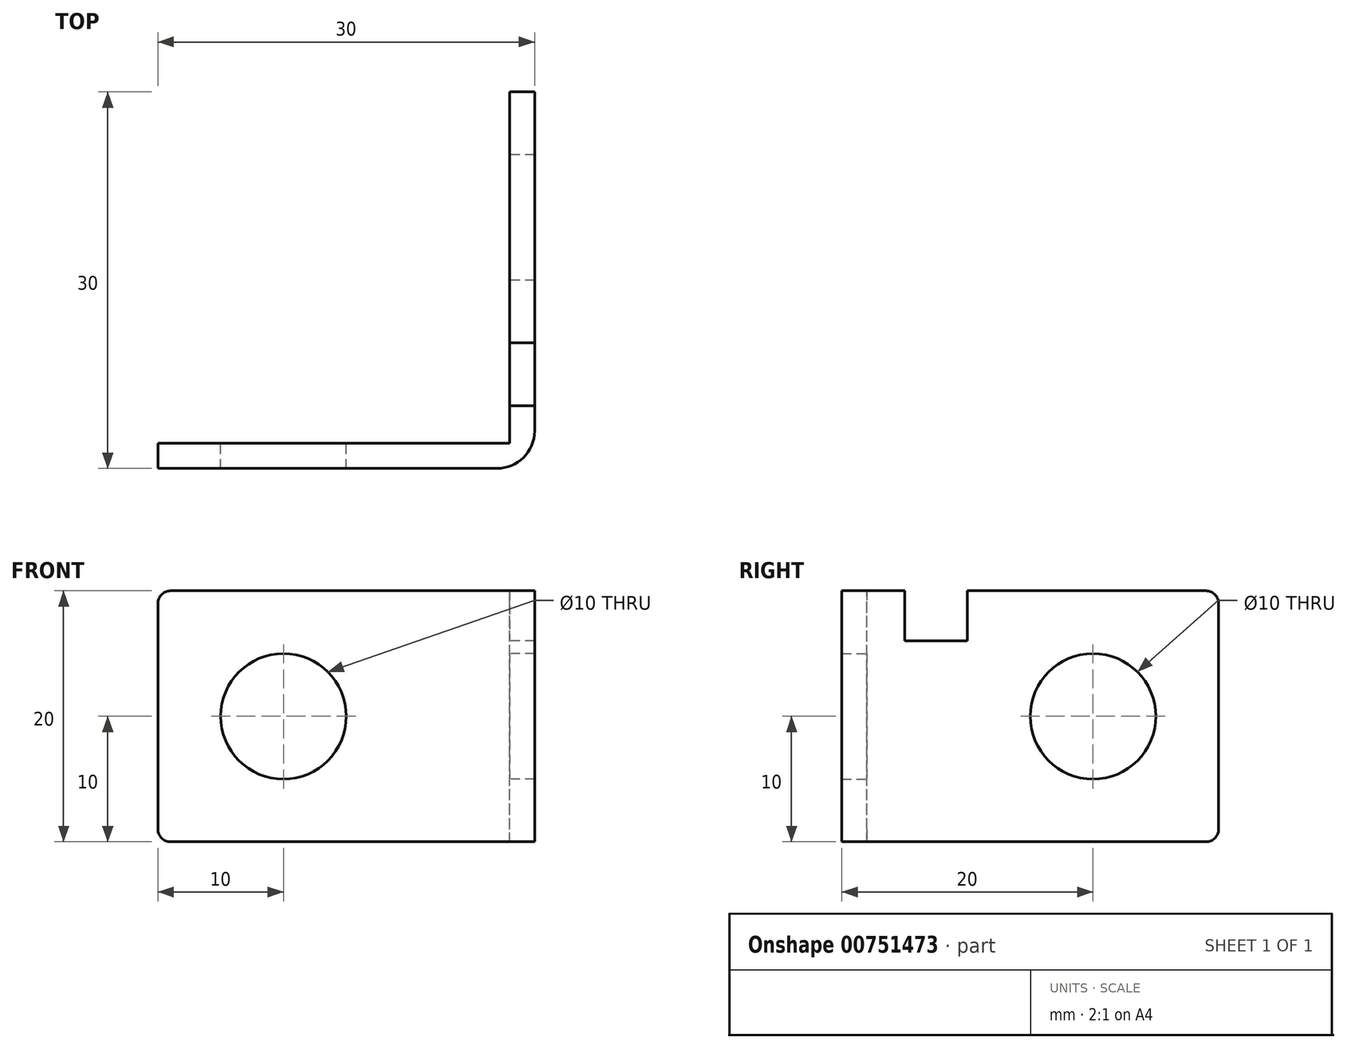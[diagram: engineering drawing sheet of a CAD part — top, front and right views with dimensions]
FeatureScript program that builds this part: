
annotation { "Feature Type Name" : "Feature", "Feature Type Description" : "" }
export const myFeature = defineFeature(function(context is Context, id is Id, definition is map)
    precondition{}
    {
        {
            var Q0;
            Q0=qCreatedBy(makeId("Front.planeOp"),FACE);
            var sketch = newSketch(context, id + "F0", { "sketchPlane" : qUnion([Q0])});
            skLineSegment(sketch, "E0.bottom", {"start": v(0, 0) * mm, "end": v(30, 0) * mm});
            skLineSegment(sketch, "E0.top", {"start": v(0, 20) * mm, "end": v(30, 20) * mm});
            skLineSegment(sketch, "E0.left", {"start": v(0, 0) * mm, "end": v(0, 20) * mm});
            skLineSegment(sketch, "E0.right", {"start": v(30, 0) * mm, "end": v(30, 20) * mm});
            skSolve(sketch);
        }
        {
            var Q0;
            Q0=makeQuery(id+"F0.imprint","IMPRINT",FACE,{"disambiguationData":[TD([[makeQuery(id+"F0.imprint","IMPRINT",EDGE,{"derivedFrom":sQuery(id+"F0.wireOp",EDGE,"E0.bottom")}),1.0]])]});
            extrude(context, id + "F1", {"entities" : qUnion([Q0]), "oppositeDirection" : true, "depth" : 2 * mm, "offsetDistance" : 25 * mm});
        }
        {
            var Q0;
            Q0=makeQuery(id+"F1.opExtrude","CAP_FACE",FACE,{"disambiguationData":[OSD([sQuery(id+"F0.wireOp",EDGE,"E0.bottom"),sQuery(id+"F0.wireOp",EDGE,"E0.top"),sQuery(id+"F0.wireOp",EDGE,"E0.left"),sQuery(id+"F0.wireOp",EDGE,"E0.right")])],"isStart":false});
            var sketch = newSketch(context, id + "F2", { "sketchPlane" : qUnion([Q0])});
            skLineSegment(sketch, "E1.bottom", {"start": v(-30, 0) * mm, "end": v(-28, 0) * mm});
            skLineSegment(sketch, "E1.top", {"start": v(-30, 20) * mm, "end": v(-28, 20) * mm});
            skLineSegment(sketch, "E1.left", {"start": v(-30, 0) * mm, "end": v(-30, 20) * mm});
            skLineSegment(sketch, "E1.right", {"start": v(-28, 0) * mm, "end": v(-28, 20) * mm});
            skSolve(sketch);
        }
        {
            var Q0;
            Q0 = qSketchRegion(id + "F2", true);
            extrude(context, id + "F3", {"entities" : qUnion([Q0]), "operationType" : NewBodyOperationType.ADD, "depth" : 28 * mm, "offsetDistance" : 25 * mm});
        }
        {
            var Q0;
            Q0=makeQuery(id+"F1.opExtrude","CAP_FACE",FACE,{"disambiguationData":[OSD([sQuery(id+"F0.wireOp",EDGE,"E0.bottom"),sQuery(id+"F0.wireOp",EDGE,"E0.top"),sQuery(id+"F0.wireOp",EDGE,"E0.left"),sQuery(id+"F0.wireOp",EDGE,"E0.right")])],"isStart":false});
            var sketch = newSketch(context, id + "F4", { "sketchPlane" : qUnion([Q0])});
            skCircle(sketch, "E2", {"center": v(-10, 10) * mm, "radius": 5 * mm});
            skSolve(sketch);
        }
        {
            var Q0;
            Q0 = qSketchRegion(id + "F4", true);
            extrude(context, id + "F5", {"entities" : qUnion([Q0]), "operationType" : NewBodyOperationType.REMOVE, "endBound" : BoundingType.UP_TO_NEXT, "oppositeDirection" : true, "depth" : 25 * mm, "offsetDistance" : 25 * mm});
        }
        {
            var Q0;
            Q0=makeQuery(id+"F3.opExtrude","SWEPT_FACE",FACE,{"disambiguationData":[OSD([sQuery(id+"F2.wireOp",EDGE,"E1.right")])]});
            var sketch = newSketch(context, id + "F6", { "sketchPlane" : qUnion([Q0])});
            skCircle(sketch, "E3", {"center": v(-20, 10) * mm, "radius": 5 * mm});
            skSolve(sketch);
        }
        {
            var Q0;
            Q0 = qSketchRegion(id + "F6", true);
            extrude(context, id + "F7", {"entities" : qUnion([Q0]), "operationType" : NewBodyOperationType.REMOVE, "endBound" : BoundingType.UP_TO_NEXT, "oppositeDirection" : true, "depth" : 25 * mm, "offsetDistance" : 25 * mm});
        }
        {
            var Q0;
            Q0=makeQuery(id+"F3.opExtrude","SWEPT_FACE",FACE,{"disambiguationData":[OSD([sQuery(id+"F2.wireOp",EDGE,"E1.right")])]});
            var sketch = newSketch(context, id + "F8", { "sketchPlane" : qUnion([Q0])});
            skLineSegment(sketch, "E4.bottom", {"start": v(-10, 20) * mm, "end": v(-5, 20) * mm});
            skLineSegment(sketch, "E4.top", {"start": v(-10, 16) * mm, "end": v(-5, 16) * mm});
            skLineSegment(sketch, "E4.left", {"start": v(-10, 20) * mm, "end": v(-10, 16) * mm});
            skLineSegment(sketch, "E4.right", {"start": v(-5, 20) * mm, "end": v(-5, 16) * mm});
            skSolve(sketch);
        }
        {
            var Q0;
            Q0 = qSketchRegion(id + "F8", true);
            extrude(context, id + "F9", {"entities" : qUnion([Q0]), "operationType" : NewBodyOperationType.REMOVE, "endBound" : BoundingType.UP_TO_NEXT, "oppositeDirection" : true, "depth" : 25 * mm, "offsetDistance" : 25 * mm});
        }
        {
            var Q0;
            Q0=makeQuery(id+"F3.opExtrude","CAP_EDGE",EDGE,{"disambiguationData":[OSD([sQuery(id+"F2.wireOp",EDGE,"E1.right")])],"isStart":true});
            var Q1;
            Q1=makeQuery(id+"F1.opExtrude","SWEPT_EDGE",EDGE,{"disambiguationData":[OSD([sQuery(id+"F0.wireOp",EDGE,"E0.top"),sQuery(id+"F0.wireOp",EDGE,"E0.left")])]});
            var Q2;
            Q2=makeQuery(id+"F1.opExtrude","SWEPT_EDGE",EDGE,{"disambiguationData":[OSD([sQuery(id+"F0.wireOp",EDGE,"E0.bottom"),sQuery(id+"F0.wireOp",EDGE,"E0.left")])]});
            var Q3;
            Q3=makeQuery(id+"F3.opExtrude","CAP_EDGE",EDGE,{"disambiguationData":[OSD([sQuery(id+"F2.wireOp",EDGE,"E1.top")])],"isStart":false});
            var Q4;
            Q4=makeQuery(id+"F3.opExtrude","CAP_EDGE",EDGE,{"disambiguationData":[OSD([sQuery(id+"F2.wireOp",EDGE,"E1.bottom")])],"isStart":false});
            fillet(context, id + "F10", {"entities" : qUnion([Q0, Q1, Q2, Q3, Q4]), "radius" : 1 * mm, "tangentPropagation" : true, "allowEdgeOverflow" : false});
        }
        {
            var Q0;
            Q0=makeQuery(id+"F1.opExtrude","CAP_EDGE",EDGE,{"disambiguationData":[OSD([sQuery(id+"F0.wireOp",EDGE,"E0.right")])],"isStart":true});
            fillet(context, id + "F11", {"entities" : qUnion([Q0]), "radius" : 3 * mm, "tangentPropagation" : true, "allowEdgeOverflow" : false});
        }
    });
